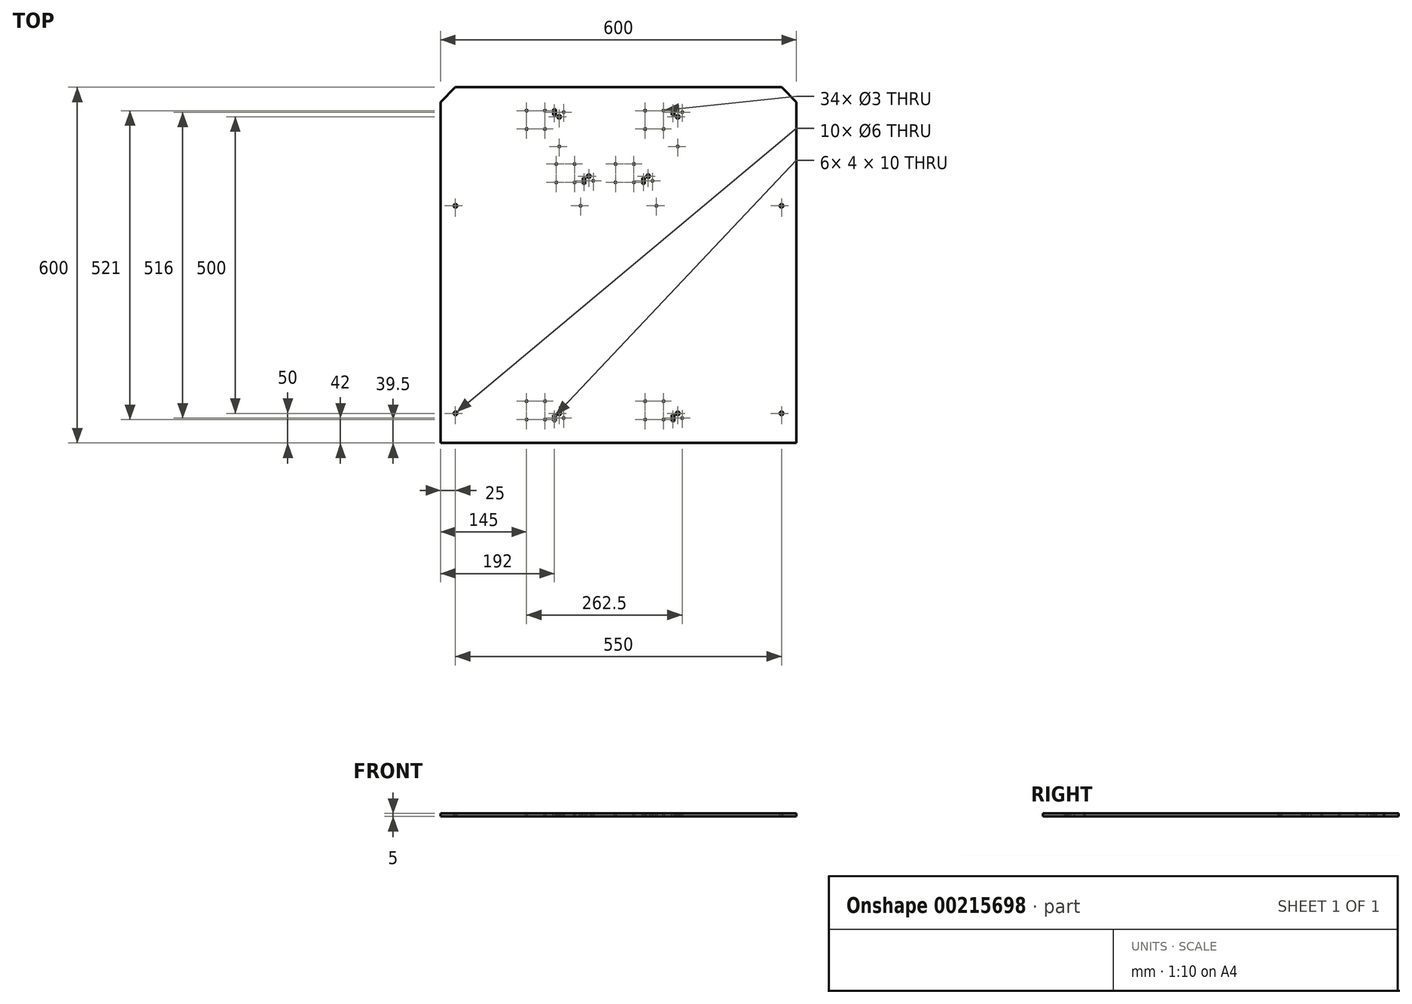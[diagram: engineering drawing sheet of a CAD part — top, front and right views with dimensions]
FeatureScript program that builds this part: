
annotation { "Feature Type Name" : "Feature", "Feature Type Description" : "" }
export const myFeature = defineFeature(function(context is Context, id is Id, definition is map)
    precondition{}
    {
        {
            var Q0;
            Q0=qCreatedBy(makeId("Top.planeOp"),FACE);
            var sketch = newSketch(context, id + "F0", { "sketchPlane" : qUnion([Q0])});
            skLineSegment(sketch, "E0.bottom", {"start": v(-300, 300) * mm, "end": v(300, 300) * mm});
            skLineSegment(sketch, "E0.top", {"start": v(-300, -300) * mm, "end": v(300, -300) * mm});
            skLineSegment(sketch, "E0.left", {"start": v(-300, 300) * mm, "end": v(-300, -300) * mm});
            skLineSegment(sketch, "E0.right", {"start": v(300, 300) * mm, "end": v(300, -300) * mm});
            skSolve(sketch);
        }
        {
            var Q0;
            Q0=makeQuery(id+"F0.imprint","IMPRINT",FACE,{"disambiguationData":[TD([[makeQuery(id+"F0.imprint","IMPRINT",EDGE,{"derivedFrom":sQuery(id+"F0.wireOp",EDGE,"E0.bottom")}),-1.0]])]});
            extrude(context, id + "F1", {"entities" : qUnion([Q0]), "depth" : 5 * mm});
        }
        {
            var Q0;
            Q0=makeQuery(id+"F1.opExtrude","CAP_FACE",FACE,{"disambiguationData":[OSD([sQuery(id+"F0.wireOp",EDGE,"E0.bottom"),sQuery(id+"F0.wireOp",EDGE,"E0.top"),sQuery(id+"F0.wireOp",EDGE,"E0.left"),sQuery(id+"F0.wireOp",EDGE,"E0.right")])],"isStart":false});
            var sketch = newSketch(context, id + "F2", { "sketchPlane" : qUnion([Q0])});
            skCircle(sketch, "E1", {"center": v(-155, -229.5) * mm, "radius": 1.5 * mm});
            skCircle(sketch, "E2.MirrorC", {"center": v(-155, -260.5) * mm, "radius": 1.5 * mm});
            skCircle(sketch, "E3.MirrorC", {"center": v(-124, -229.5) * mm, "radius": 1.5 * mm});
            skCircle(sketch, "E4.MirrorC", {"center": v(-124, -260.5) * mm, "radius": 1.5 * mm});
            skCircle(sketch, "E5", {"center": v(-100, -250) * mm, "radius": 3 * mm});
            skLineSegment(sketch, "E6.bottom", {"start": v(-110, -253) * mm, "end": v(-106, -253) * mm});
            skLineSegment(sketch, "E6.top", {"start": v(-110, -263) * mm, "end": v(-106, -263) * mm});
            skLineSegment(sketch, "E6.left", {"start": v(-110, -253) * mm, "end": v(-110, -263) * mm});
            skLineSegment(sketch, "E6.right", {"start": v(-106, -253) * mm, "end": v(-106, -263) * mm});
            skCircle(sketch, "E7", {"center": v(-92.5, -258) * mm, "radius": 1.5 * mm});
            skPoint(sketch, "E8", {"position": v(-106, -258) * mm});
            skLineSegment(sketch, "E9", {"start": v(-115, -229.5) * mm, "end": v(-115, -260.5) * mm, "construction": true});
            skLineSegment(sketch, "E10", {"start": v(-139.5, -229.5) * mm, "end": v(-139.5, -260.5) * mm, "construction": true});
            skLineSegment(sketch, "E11", {"start": v(-164, -245) * mm, "end": v(-115, -245) * mm, "construction": true});
            skCircle(sketch, "E12", {"center": v(45, -229.5) * mm, "radius": 1.5 * mm});
            skCircle(sketch, "E13.MirrorC", {"center": v(45, -260.5) * mm, "radius": 1.5 * mm});
            skCircle(sketch, "E14.MirrorC", {"center": v(76, -229.5) * mm, "radius": 1.5 * mm});
            skCircle(sketch, "E15.MirrorC", {"center": v(76, -260.5) * mm, "radius": 1.5 * mm});
            skCircle(sketch, "E16", {"center": v(100, -250) * mm, "radius": 3 * mm});
            skLineSegment(sketch, "E17.bottom", {"start": v(90, -253) * mm, "end": v(94, -253) * mm});
            skLineSegment(sketch, "E17.top", {"start": v(90, -263) * mm, "end": v(94, -263) * mm});
            skLineSegment(sketch, "E17.left", {"start": v(90, -253) * mm, "end": v(90, -263) * mm});
            skLineSegment(sketch, "E17.right", {"start": v(94, -253) * mm, "end": v(94, -263) * mm});
            skCircle(sketch, "E18", {"center": v(107.5, -258) * mm, "radius": 1.5 * mm});
            skPoint(sketch, "E19", {"position": v(94, -258) * mm});
            skLineSegment(sketch, "E20", {"start": v(85, -229.5) * mm, "end": v(85, -260.5) * mm, "construction": true});
            skLineSegment(sketch, "E21", {"start": v(60.5, -229.5) * mm, "end": v(60.5, -260.5) * mm, "construction": true});
            skLineSegment(sketch, "E22", {"start": v(36, -245) * mm, "end": v(85, -245) * mm, "construction": true});
            skLineSegment(sketch, "E23.MirrorCS", {"start": v(90, 253) * mm, "end": v(94, 253) * mm});
            skLineSegment(sketch, "E24.MirrorCS", {"start": v(-110, 253) * mm, "end": v(-106, 253) * mm});
            skLineSegment(sketch, "E25.MirrorCS", {"start": v(90, 253) * mm, "end": v(90, 263) * mm});
            skLineSegment(sketch, "E26.MirrorCS", {"start": v(90, 263) * mm, "end": v(94, 263) * mm});
            skLineSegment(sketch, "E27.MirrorCS", {"start": v(94, 253) * mm, "end": v(94, 263) * mm});
            skLineSegment(sketch, "E28.MirrorCS", {"start": v(-106, 253) * mm, "end": v(-106, 263) * mm});
            skLineSegment(sketch, "E29.MirrorCS", {"start": v(-110, 253) * mm, "end": v(-110, 263) * mm});
            skLineSegment(sketch, "E30.MirrorCS", {"start": v(-110, 263) * mm, "end": v(-106, 263) * mm});
            skCircle(sketch, "E31.MirrorC", {"center": v(100, 250) * mm, "radius": 3 * mm});
            skCircle(sketch, "E32.MirrorC", {"center": v(76, 229.5) * mm, "radius": 1.5 * mm});
            skCircle(sketch, "E33.MirrorC", {"center": v(76, 260.5) * mm, "radius": 1.5 * mm});
            skLineSegment(sketch, "E34.MirrorCS", {"start": v(85, 229.5) * mm, "end": v(85, 260.5) * mm, "construction": true});
            skCircle(sketch, "E35.MirrorC", {"center": v(-124, 260.5) * mm, "radius": 1.5 * mm});
            skCircle(sketch, "E36.MirrorC", {"center": v(-124, 229.5) * mm, "radius": 1.5 * mm});
            skCircle(sketch, "E37.MirrorC", {"center": v(-100, 250) * mm, "radius": 3 * mm});
            skCircle(sketch, "E38.MirrorC", {"center": v(107.5, 258) * mm, "radius": 1.5 * mm});
            skLineSegment(sketch, "E39.MirrorCS", {"start": v(-115, 229.5) * mm, "end": v(-115, 260.5) * mm, "construction": true});
            skCircle(sketch, "E40.MirrorC", {"center": v(-92.5, 258) * mm, "radius": 1.5 * mm});
            skCircle(sketch, "E41.MirrorC", {"center": v(-155, 229.5) * mm, "radius": 1.5 * mm});
            skCircle(sketch, "E42.MirrorC", {"center": v(45, 229.5) * mm, "radius": 1.5 * mm});
            skCircle(sketch, "E43.MirrorC", {"center": v(45, 260.5) * mm, "radius": 1.5 * mm});
            skPoint(sketch, "E44.MirrorP", {"position": v(94, 258) * mm});
            skLineSegment(sketch, "E45.MirrorCS", {"start": v(-139.5, 229.5) * mm, "end": v(-139.5, 260.5) * mm, "construction": true});
            skPoint(sketch, "E46.MirrorP", {"position": v(-106, 258) * mm});
            skCircle(sketch, "E47.MirrorC", {"center": v(-155, 260.5) * mm, "radius": 1.5 * mm});
            skLineSegment(sketch, "E48.MirrorCS", {"start": v(60.5, 229.5) * mm, "end": v(60.5, 260.5) * mm, "construction": true});
            skLineSegment(sketch, "E49.MirrorCS", {"start": v(36, 245) * mm, "end": v(85, 245) * mm, "construction": true});
            skLineSegment(sketch, "E50.MirrorCS", {"start": v(-164, 245) * mm, "end": v(-115, 245) * mm, "construction": true});
            skCircle(sketch, "E51", {"center": v(-100, 200) * mm, "radius": 1.5 * mm});
            skCircle(sketch, "E52", {"center": v(100, 200) * mm, "radius": 1.5 * mm});
            skCircle(sketch, "E53", {"center": v(-105, 170.5) * mm, "radius": 1.5 * mm});
            skCircle(sketch, "E54.MirrorC", {"center": v(-105, 139.5) * mm, "radius": 1.5 * mm});
            skCircle(sketch, "E55.MirrorC", {"center": v(-74, 170.5) * mm, "radius": 1.5 * mm});
            skCircle(sketch, "E56.MirrorC", {"center": v(-74, 139.5) * mm, "radius": 1.5 * mm});
            skCircle(sketch, "E57", {"center": v(-50, 150) * mm, "radius": 3 * mm});
            skLineSegment(sketch, "E58.bottom", {"start": v(-60, 147) * mm, "end": v(-56, 147) * mm});
            skLineSegment(sketch, "E58.top", {"start": v(-60, 137) * mm, "end": v(-56, 137) * mm});
            skLineSegment(sketch, "E58.left", {"start": v(-60, 147) * mm, "end": v(-60, 137) * mm});
            skLineSegment(sketch, "E58.right", {"start": v(-56, 147) * mm, "end": v(-56, 137) * mm});
            skCircle(sketch, "E59", {"center": v(-42.5, 142) * mm, "radius": 1.5 * mm});
            skPoint(sketch, "E60", {"position": v(-56, 142) * mm});
            skLineSegment(sketch, "E61", {"start": v(-65, 170.5) * mm, "end": v(-65, 139.5) * mm, "construction": true});
            skLineSegment(sketch, "E62", {"start": v(-89.5, 170.5) * mm, "end": v(-89.5, 139.5) * mm, "construction": true});
            skLineSegment(sketch, "E63", {"start": v(-114, 155) * mm, "end": v(-65, 155) * mm, "construction": true});
            skCircle(sketch, "E64", {"center": v(-5, 170.5) * mm, "radius": 1.5 * mm});
            skCircle(sketch, "E65.MirrorC", {"center": v(-5, 139.5) * mm, "radius": 1.5 * mm});
            skCircle(sketch, "E66.MirrorC", {"center": v(26, 170.5) * mm, "radius": 1.5 * mm});
            skCircle(sketch, "E67.MirrorC", {"center": v(26, 139.5) * mm, "radius": 1.5 * mm});
            skCircle(sketch, "E68", {"center": v(50, 150) * mm, "radius": 3 * mm});
            skLineSegment(sketch, "E69.bottom", {"start": v(40, 147) * mm, "end": v(44, 147) * mm});
            skLineSegment(sketch, "E69.top", {"start": v(40, 137) * mm, "end": v(44, 137) * mm});
            skLineSegment(sketch, "E69.left", {"start": v(40, 147) * mm, "end": v(40, 137) * mm});
            skLineSegment(sketch, "E69.right", {"start": v(44, 147) * mm, "end": v(44, 137) * mm});
            skCircle(sketch, "E70", {"center": v(57.5, 142) * mm, "radius": 1.5 * mm});
            skPoint(sketch, "E71", {"position": v(44, 142) * mm});
            skLineSegment(sketch, "E72", {"start": v(35, 170.5) * mm, "end": v(35, 139.5) * mm, "construction": true});
            skLineSegment(sketch, "E73", {"start": v(10.5, 170.5) * mm, "end": v(10.5, 139.5) * mm, "construction": true});
            skLineSegment(sketch, "E74", {"start": v(-14, 155) * mm, "end": v(35, 155) * mm, "construction": true});
            skLineSegment(sketch, "E75.bottom", {"start": v(-75, 110) * mm, "end": v(75, 110) * mm, "construction": true});
            skLineSegment(sketch, "E75.top", {"start": v(-75, -120) * mm, "end": v(75, -120) * mm, "construction": true});
            skLineSegment(sketch, "E75.left", {"start": v(-75, 110) * mm, "end": v(-75, -120) * mm, "construction": true});
            skLineSegment(sketch, "E75.right", {"start": v(75, 110) * mm, "end": v(75, -120) * mm, "construction": true});
            skCircle(sketch, "E76", {"center": v(-64, 100) * mm, "radius": 1.5 * mm});
            skCircle(sketch, "E77.MirrorC", {"center": v(64, 100) * mm, "radius": 1.5 * mm});
            skLineSegment(sketch, "E78", {"start": v(-275, 300) * mm, "end": v(-275, -300) * mm, "construction": true});
            skCircle(sketch, "E79", {"center": v(-275, -250) * mm, "radius": 3 * mm});
            skLineSegment(sketch, "E80", {"start": v(-300, 150) * mm, "end": v(300, 150) * mm, "construction": true});
            skCircle(sketch, "E81", {"center": v(-275, 100) * mm, "radius": 3 * mm});
            skCircle(sketch, "E82.MirrorC", {"center": v(275, 100) * mm, "radius": 3 * mm});
            skCircle(sketch, "E83.MirrorC", {"center": v(275, -250) * mm, "radius": 3 * mm});
            skLineSegment(sketch, "E84", {"start": v(-275, 300) * mm, "end": v(-300, 275) * mm});
            skLineSegment(sketch, "E85", {"start": v(-300, 275) * mm, "end": v(-300, 300) * mm});
            skLineSegment(sketch, "E86", {"start": v(-300, 300) * mm, "end": v(-275, 300) * mm});
            skLineSegment(sketch, "E87.MirrorCS", {"start": v(275, 300) * mm, "end": v(300, 275) * mm});
            skLineSegment(sketch, "E88.MirrorCS", {"start": v(300, 300) * mm, "end": v(275, 300) * mm});
            skLineSegment(sketch, "E89.MirrorCS", {"start": v(300, 275) * mm, "end": v(300, 300) * mm});
            skLineSegment(sketch, "E90", {"start": v(-300, -150) * mm, "end": v(300, -150) * mm, "construction": true});
            skSolve(sketch);
        }
        {
            var Q0;
            Q0=qSketchRegion(id+"F2",true);
            extrude(context, id + "F3", {"entities" : qUnion([Q0]), "operationType" : NewBodyOperationType.REMOVE, "endBound" : BoundingType.THROUGH_ALL, "oppositeDirection" : true, "depth" : 25 * mm});
        }
    });
